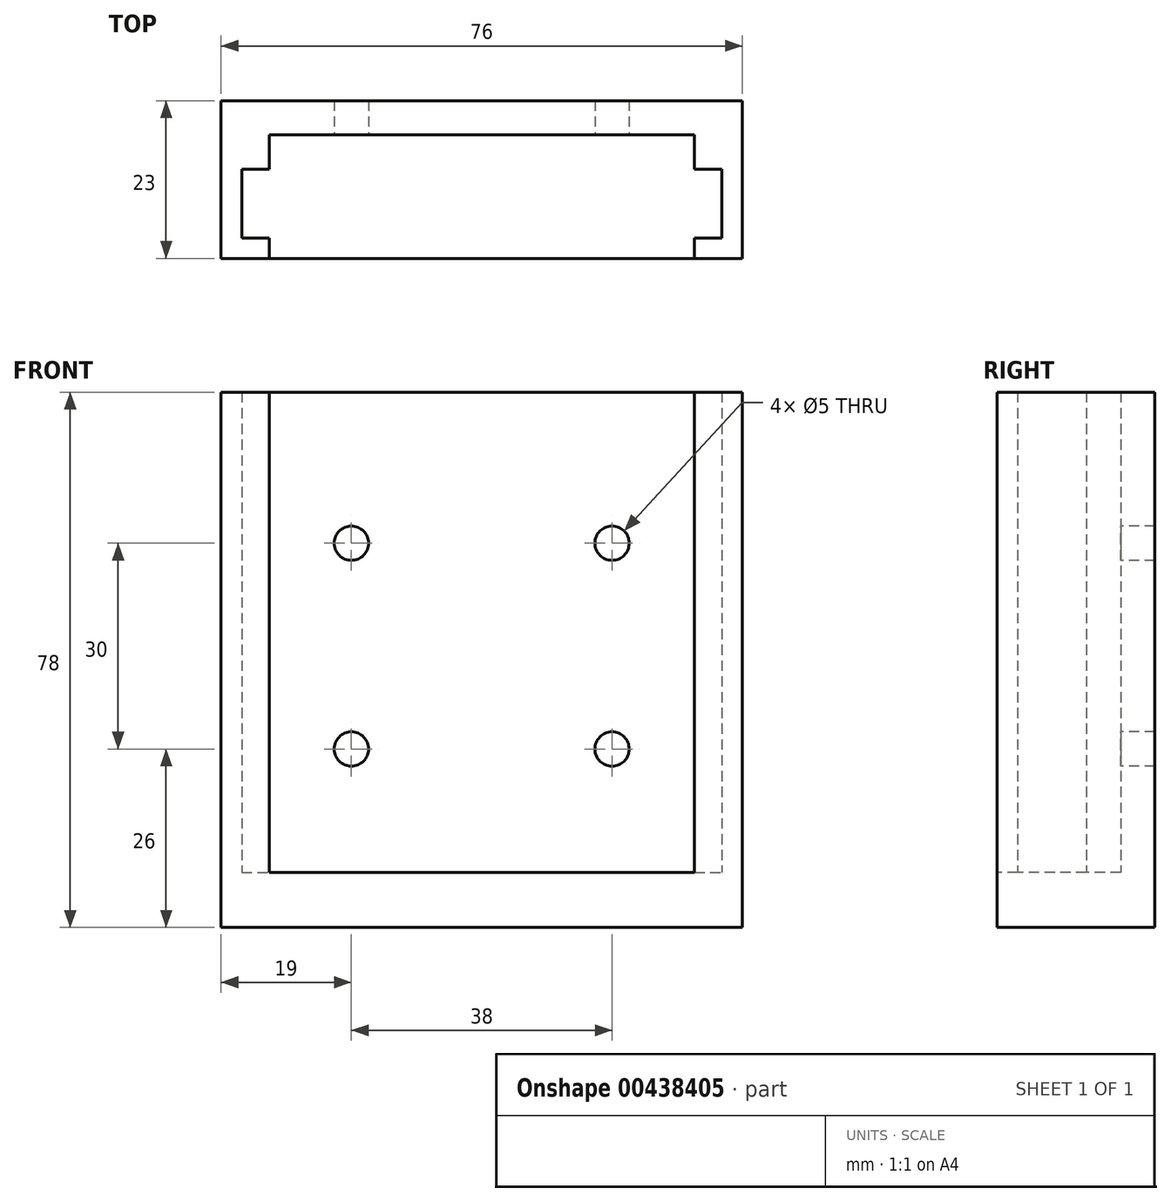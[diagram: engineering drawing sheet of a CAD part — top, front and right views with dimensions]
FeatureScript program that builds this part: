
annotation { "Feature Type Name" : "Feature", "Feature Type Description" : "" }
export const myFeature = defineFeature(function(context is Context, id is Id, definition is map)
    precondition{}
    {
        {
            var Q0;
            Q0=qCreatedBy(makeId("Top.planeOp"),FACE);
            var sketch = newSketch(context, id + "F0", { "sketchPlane" : qUnion([Q0])});
            skLineSegment(sketch, "E0.bottom", {"start": v(-39.67, 1.34) * mm, "end": v(36.33, 1.34) * mm});
            skLineSegment(sketch, "E0.top", {"start": v(-39.67, -21.66) * mm, "end": v(36.33, -21.66) * mm});
            skLineSegment(sketch, "E0.left", {"start": v(-39.67, 1.34) * mm, "end": v(-39.67, -21.66) * mm});
            skLineSegment(sketch, "E0.right", {"start": v(36.33, 1.34) * mm, "end": v(36.33, -21.66) * mm});
            skSolve(sketch);
        }
        {
            var Q0;
            Q0=makeQuery(id+"F0.imprint","IMPRINT",FACE,{"disambiguationData":[TD([[makeQuery(id+"F0.imprint","IMPRINT",EDGE,{"derivedFrom":sQuery(id+"F0.wireOp",EDGE,"E0.bottom")}),-1.0]])]});
            extrude(context, id + "F1", {"entities" : qUnion([Q0]), "depth" : 8 * mm});
        }
        {
            var Q0;
            Q0=makeQuery(id+"F1.opExtrude","CAP_FACE",FACE,{"disambiguationData":[OSD([sQuery(id+"F0.wireOp",EDGE,"E0.bottom"),sQuery(id+"F0.wireOp",EDGE,"E0.top"),sQuery(id+"F0.wireOp",EDGE,"E0.left"),sQuery(id+"F0.wireOp",EDGE,"E0.right")])],"isStart":false});
            var sketch = newSketch(context, id + "F2", { "sketchPlane" : qUnion([Q0])});
            skLineSegment(sketch, "E1", {"start": v(-39.67, -21.66) * mm, "end": v(-39.67, 1.34) * mm});
            skLineSegment(sketch, "E2", {"start": v(-39.67, 1.34) * mm, "end": v(36.33, 1.34) * mm});
            skLineSegment(sketch, "E3", {"start": v(36.33, 1.34) * mm, "end": v(36.33, -21.66) * mm});
            skLineSegment(sketch, "E4", {"start": v(36.33, -21.66) * mm, "end": v(29.33, -21.66) * mm});
            skLineSegment(sketch, "E5", {"start": v(29.33, -21.66) * mm, "end": v(29.33, -18.66) * mm});
            skLineSegment(sketch, "E6", {"start": v(29.33, -18.66) * mm, "end": v(33.33, -18.66) * mm});
            skLineSegment(sketch, "E7", {"start": v(-36.67, -18.66) * mm, "end": v(-32.67, -18.66) * mm});
            skLineSegment(sketch, "E8", {"start": v(-32.67, -18.66) * mm, "end": v(-32.67, -21.66) * mm});
            skLineSegment(sketch, "E9", {"start": v(-32.67, -21.66) * mm, "end": v(-39.67, -21.66) * mm});
            skLineSegment(sketch, "E10", {"start": v(-36.67, -8.66) * mm, "end": v(-32.67, -8.66) * mm});
            skLineSegment(sketch, "E11", {"start": v(-32.67, -8.66) * mm, "end": v(-32.67, -3.66) * mm});
            skLineSegment(sketch, "E12", {"start": v(29.33, -3.66) * mm, "end": v(29.33, -8.66) * mm});
            skLineSegment(sketch, "E13", {"start": v(29.33, -8.66) * mm, "end": v(33.33, -8.66) * mm});
            skLineSegment(sketch, "E14", {"start": v(-36.67, -8.66) * mm, "end": v(-36.67, -18.66) * mm});
            skLineSegment(sketch, "E15", {"start": v(-32.67, -3.66) * mm, "end": v(29.33, -3.66) * mm});
            skLineSegment(sketch, "E16", {"start": v(33.33, -8.66) * mm, "end": v(33.33, -18.66) * mm});
            skSolve(sketch);
        }
        {
            var Q0;
            Q0=makeQuery(id+"F2.imprint","IMPRINT",FACE,{"disambiguationData":[TD([[makeQuery(id+"F2.imprint","IMPRINT",EDGE,{"derivedFrom":sQuery(id+"F2.wireOp",EDGE,"E1")}),1.0]])]});
            extrude(context, id + "F3", {"entities" : qUnion([Q0]), "operationType" : NewBodyOperationType.ADD, "depth" : 70 * mm});
        }
        {
            var Q0;
            Q0=makeQuery(id+"F3.opExtrude","SWEPT_FACE",FACE,{"disambiguationData":[OSD([sQuery(id+"F2.wireOp",EDGE,"E15")])]});
            var sketch = newSketch(context, id + "F4", { "sketchPlane" : qUnion([Q0])});
            skCircle(sketch, "E17", {"center": v(-20.67, 56) * mm, "radius": 2.5 * mm});
            skCircle(sketch, "E18", {"center": v(17.33, 56) * mm, "radius": 2.5 * mm});
            skCircle(sketch, "E19", {"center": v(17.33, 26) * mm, "radius": 2.5 * mm});
            skCircle(sketch, "E20", {"center": v(-20.67, 26) * mm, "radius": 2.5 * mm});
            skLineSegment(sketch, "E21", {"start": v(-1.67, 78) * mm, "end": v(-1.67, 8) * mm, "construction": true});
            skSolve(sketch);
        }
        {
            var Q0;
            Q0=makeQuery(id+"F4.imprint","IMPRINT",FACE,{"disambiguationData":[TD([[makeQuery(id+"F4.imprint","IMPRINT",EDGE,{"derivedFrom":sQuery(id+"F4.wireOp",EDGE,"E18")}),1.0]])]});
            var Q1;
            Q1=makeQuery(id+"F4.imprint","IMPRINT",FACE,{"disambiguationData":[TD([[makeQuery(id+"F4.imprint","IMPRINT",EDGE,{"derivedFrom":sQuery(id+"F4.wireOp",EDGE,"E17")}),1.0]])]});
            var Q2;
            Q2=makeQuery(id+"F4.imprint","IMPRINT",FACE,{"disambiguationData":[TD([[makeQuery(id+"F4.imprint","IMPRINT",EDGE,{"derivedFrom":sQuery(id+"F4.wireOp",EDGE,"E20")}),1.0]])]});
            var Q3;
            Q3=makeQuery(id+"F4.imprint","IMPRINT",FACE,{"disambiguationData":[TD([[makeQuery(id+"F4.imprint","IMPRINT",EDGE,{"derivedFrom":sQuery(id+"F4.wireOp",EDGE,"E19")}),1.0]])]});
            extrude(context, id + "F5", {"entities" : qUnion([Q0, Q1, Q2, Q3]), "operationType" : NewBodyOperationType.REMOVE, "oppositeDirection" : true, "depth" : 25 * mm});
        }
    });
